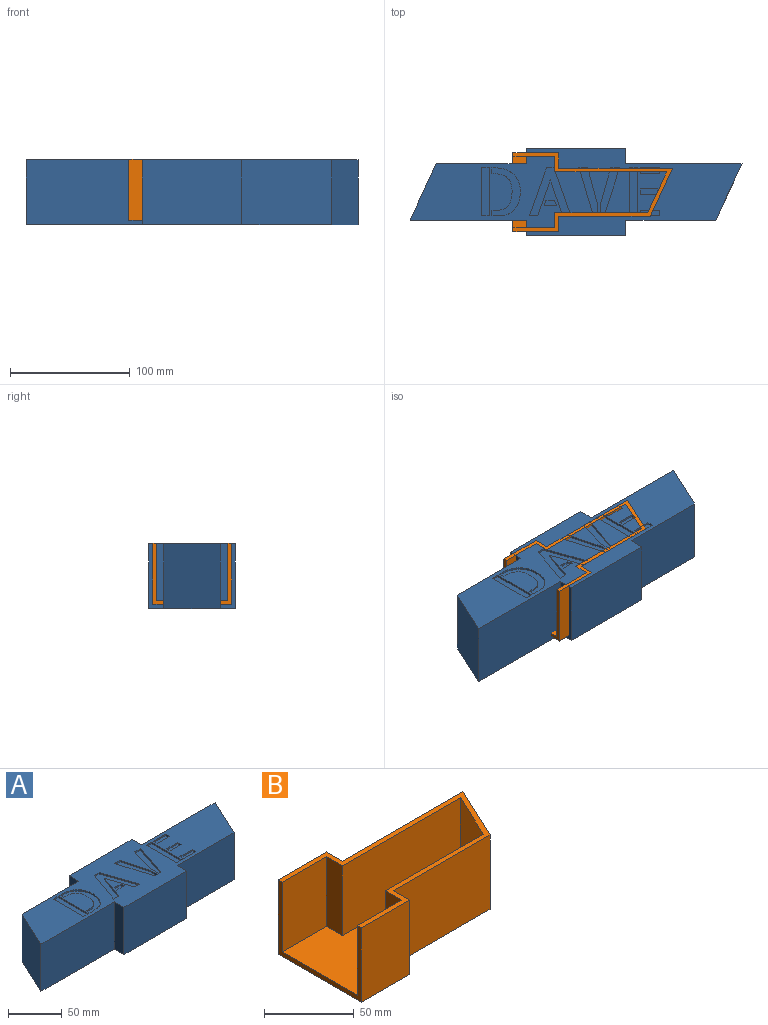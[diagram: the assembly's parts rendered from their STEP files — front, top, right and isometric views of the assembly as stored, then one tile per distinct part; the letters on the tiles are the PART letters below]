
ASSEMBLY  parts=2 mates=1
PART A: 100 faces, bbox 276.7x72.4x54 mm
  f0: plane 276.71x72.36mm, normal (0,0,1), area 11913.1mm2, adj f2,f3,f4,f5,f6,f7,f8,f9
  f1: plane 276.71x72.36mm, normal (0,0,-1), area 2063.9mm2, adj f2,f3,f4,f5,f6,f7,f8,f9
  f2: plane 83.06x53.98mm, normal (0,1,0), area 4483.1mm2, adj f0,f1,f3,f13
  f3: plane 53.98x12.7mm, normal (-1,0,0), area 685.5mm2, adj f0,f1,f2,f4
  f4: plane 74.93x53.98mm, normal (0,1,0), area 4044.3mm2, adj f0,f1,f3,f5
  f5: plane 53.98x46.96mm, normal (-0.91,0.42,0), area 2796.8mm2, adj f0,f1,f4,f6
  f6: plane 96.83x53.98mm, normal (0,-1,0), area 5226.3mm2, adj f0,f1,f5,f7
  f7: plane 53.98x12.7mm, normal (-1,0,0), area 685.5mm2, adj f0,f1,f6,f8
  f8: plane 83.06x53.98mm, normal (0,-1,0), area 4483.1mm2, adj f0,f1,f7,f9
  f9: plane 53.98x12.7mm, normal (1,0,0), area 685.5mm2, adj f0,f1,f8,f10
  f10: plane 74.93x53.98mm, normal (0,-1,0), area 4044.3mm2, adj f0,f1,f9,f11
  f11: plane 53.98x46.96mm, normal (0.91,-0.42,0), area 2796.8mm2, adj f0,f1,f10,f12
  f12: plane 96.83x53.98mm, normal (0,1,0), area 5226.3mm2, adj f0,f1,f11,f13
  f13: plane 53.98x12.7mm, normal (1,0,0), area 685.5mm2, adj f0,f1,f2,f12
  f14: plane 76.71x50.8mm, normal (0,-1,0), area 3896.8mm2, adj f1,f15,f25,f26
  f15: plane 50.8x12.7mm, normal (1,0,0), area 645.2mm2, adj f1,f14,f16,f26
  f16: plane 76.08x50.8mm, normal (0,-1,0), area 3865mm2, adj f1,f15,f17,f26
  f17: plane 50.8x40.61mm, normal (0.91,-0.42,0), area 2276.3mm2, adj f1,f16,f18,f26
  f18: plane 95.02x50.8mm, normal (0,1,0), area 4827mm2, adj f1,f17,f19,f26
  f19: plane 50.8x12.7mm, normal (1,0,0), area 645.2mm2, adj f1,f18,f20,f26
  f20: plane 76.71x50.8mm, normal (0,1,0), area 3896.8mm2, adj f1,f19,f21,f26
  f21: plane 50.8x12.7mm, normal (-1,0,0), area 645.2mm2, adj f1,f20,f22,f26
  f22: plane 76.08x50.8mm, normal (0,1,0), area 3865mm2, adj f1,f21,f23,f26
  f23: plane 50.8x40.61mm, normal (-0.91,0.42,0), area 2276.3mm2, adj f1,f22,f24,f26
  f24: plane 95.02x50.8mm, normal (0,-1,0), area 4827mm2, adj f1,f23,f25,f26
  f25: plane 50.8x12.7mm, normal (-1,0,0), area 645.2mm2, adj f1,f14,f24,f26
  f26: plane 266.75x66.01mm, normal (0,0,-1), area 12012.3mm2, adj f14,f15,f16,f17,f18,f19,f20,f21
  f27: plane 7.44x1.59mm, normal (0,-1,0), area 11.8mm2, adj f0,f28,f31,f32
  f28: plane 40.27x12.44mm, normal (0.96,0.3,0), area 66.9mm2, adj f0,f27,f29,f32
  f29: plane 3.43x1.59mm, normal (0,1,0), area 5.4mm2, adj f0,f28,f30,f32
  f30: plane 8.86x1.59mm, normal (-1,0,0), area 14.1mm2, adj f0,f29,f31,f32
  f31: plane 31.41x8.43mm, normal (-0.97,-0.26,0), area 51.6mm2, adj f0,f27,f30,f32
  f32: plane 40.27x15.87mm, normal (0,0,1), area 256.2mm2, adj f27,f28,f29,f30,f31
  f33: plane 4.41x1.59mm, normal (-0.94,-0.34,0), area 7.4mm2, adj f0,f34,f36,f37
  f34: plane 7.29x1.59mm, normal (0,-1,0), area 11.6mm2, adj f0,f33,f35,f37
  f35: plane 4.41x1.59mm, normal (0.95,-0.33,0), area 7.4mm2, adj f0,f34,f36,f37
  f36: plane 10.38x1.59mm, normal (0,1,0), area 16.5mm2, adj f0,f33,f35,f37
  f37: plane 10.38x4.41mm, normal (0,0,1), area 38.9mm2, adj f33,f34,f35,f36
  f38: plane 6.74x1.59mm, normal (0,1,0), area 10.7mm2, adj f0,f39,f44,f45
  f39: plane 40x13.91mm, normal (-0.94,-0.33,0), area 67.2mm2, adj f0,f38,f40,f45
  f40: plane 6.47x1.59mm, normal (0,-1,0), area 10.3mm2, adj f0,f39,f41,f45
  f41: plane 40x14.02mm, normal (0.94,-0.33,0), area 67.3mm2, adj f0,f40,f42,f45
  f42: plane 6.79x1.59mm, normal (0,1,0), area 10.8mm2, adj f0,f41,f43,f45
  f43: plane 30x10.49mm, normal (-0.94,0.33,0), area 50.5mm2, adj f0,f42,f44,f45
  f44: plane 30x10.38mm, normal (0.95,0.33,0), area 50.4mm2, adj f0,f38,f43,f45
  f45: plane 40x34.4mm, normal (0,0,1), area 504.3mm2, adj f38,f39,f40,f41,f42,f43,f44
  f46: extruded ~8.88x1.6mm, area 14.4mm2, adj f0,f47,f67,f68
  f47: plane 3.32x1.59mm, normal (0,-1,0), area 5.3mm2, adj f0,f46,f48,f68
  f48: plane 4.94x1.59mm, normal (1,0,0), area 7.8mm2, adj f0,f47,f49,f68
  f49: plane 1.59x1.58mm, normal (0,1,0), area 2.5mm2, adj f0,f48,f50,f68
  f50: extruded ~7.6x1.59mm, area 12.3mm2, adj f0,f49,f51,f68
  f51: extruded ~4.65x3.21mm, area 9mm2, adj f0,f50,f52,f68
  f52: extruded ~4.43x2.31mm, area 8mm2, adj f0,f51,f53,f68
  f53: extruded ~4.95x1.59mm, area 7.9mm2, adj f0,f52,f54,f68
  f54: extruded ~12.28x2.93mm, area 20.3mm2, adj f0,f53,f55,f68
  f55: extruded ~9.56x4.24mm, area 17.3mm2, adj f0,f54,f56,f68
  f56: plane 4.24x1.59mm, normal (0,-1,0), area 6.7mm2, adj f0,f55,f57,f68
  f57: plane 4.78x1.59mm, normal (1,0,0), area 7.6mm2, adj f0,f56,f58,f68
  f58: plane 6.42x1.59mm, normal (0,1,0), area 10.2mm2, adj f0,f57,f59,f68
  f59: extruded ~2.33x1.59mm, area 3.7mm2, adj f0,f58,f60,f68
  f60: extruded ~3.48x1.59mm, area 5.7mm2, adj f0,f59,f61,f68
  f61: extruded ~3.94x2.04mm, area 7.1mm2, adj f0,f60,f62,f68
  f62: extruded ~3.72x3.67mm, area 8.3mm2, adj f0,f61,f63,f68
  f63: extruded ~5.87x2.69mm, area 10.3mm2, adj f0,f62,f64,f68
  f64: extruded ~8.45x1.59mm, area 13.6mm2, adj f0,f63,f65,f68
  f65: extruded ~6.99x1.59mm, area 11.3mm2, adj f0,f64,f66,f68
  f66: extruded ~6.06x3.78mm, area 11.4mm2, adj f0,f65,f67,f68
  f67: extruded ~6.36x4.27mm, area 12.2mm2, adj f0,f46,f66,f68
  f68: plane 40.05x23.59mm, normal (0,0,1), area 361.5mm2, adj f46,f47,f48,f49,f50,f51,f52,f53
  f69: plane 7.39x1.59mm, normal (0,-1,0), area 11.7mm2, adj f0,f70,f73,f74
  f70: plane 29.67x8.48mm, normal (0.96,-0.27,0), area 49mm2, adj f0,f69,f71,f74
  f71: plane 10.6x1.59mm, normal (1,0,0), area 16.8mm2, adj f0,f70,f72,f74
  f72: plane 2.83x1.59mm, normal (0,1,0), area 4.5mm2, adj f0,f71,f73,f74
  f73: plane 40.27x13.04mm, normal (-0.95,0.31,0), area 67.2mm2, adj f0,f69,f72,f74
  f74: plane 40.27x15.87mm, normal (0,0,1), area 250.7mm2, adj f69,f70,f71,f72,f73
  f75: plane 6.63x1.59mm, normal (0,-1,0), area 10.5mm2, adj f0,f76,f78,f79
  f76: plane 40.05x1.59mm, normal (1,0,0), area 63.6mm2, adj f0,f75,f77,f79
  f77: plane 6.63x1.59mm, normal (0,1,0), area 10.5mm2, adj f0,f76,f78,f79
  f78: plane 40.05x1.59mm, normal (-1,0,0), area 63.6mm2, adj f0,f75,f77,f79
  f79: plane 40.05x6.63mm, normal (0,0,1), area 265.4mm2, adj f75,f76,f77,f78
  f80: plane 14.5x1.59mm, normal (0,1,0), area 23mm2, adj f0,f81,f83,f84
  f81: plane 4.46x1.59mm, normal (-1,0,0), area 7.1mm2, adj f0,f80,f82,f84
  f82: plane 14.5x1.59mm, normal (0,-1,0), area 23mm2, adj f0,f81,f83,f84
  f83: plane 4.46x1.59mm, normal (1,0,0), area 7.1mm2, adj f0,f80,f82,f84
  f84: plane 14.5x4.46mm, normal (0,0,1), area 64.7mm2, adj f80,f81,f82,f83
  f85: plane 16.19x1.59mm, normal (0,-1,0), area 25.7mm2, adj f0,f86,f88,f89
  f86: plane 4.95x1.59mm, normal (1,0,0), area 7.9mm2, adj f0,f85,f87,f89
  f87: plane 16.19x1.59mm, normal (0,1,0), area 25.7mm2, adj f0,f86,f88,f89
  f88: plane 4.95x1.59mm, normal (-1,0,0), area 7.9mm2, adj f0,f85,f87,f89
  f89: plane 16.19x4.95mm, normal (0,0,1), area 80.1mm2, adj f85,f86,f87,f88
  f90: plane 4.94x1.59mm, normal (-1,0,0), area 7.8mm2, adj f0,f91,f93,f94
  f91: plane 16.19x1.59mm, normal (0,-1,0), area 25.7mm2, adj f0,f90,f92,f94
  f92: plane 4.94x1.59mm, normal (1,0,0), area 7.8mm2, adj f0,f91,f93,f94
  f93: plane 16.19x1.59mm, normal (0,1,0), area 25.7mm2, adj f0,f90,f92,f94
  f94: plane 16.19x4.94mm, normal (0,0,1), area 80mm2, adj f90,f91,f92,f93
  f95: plane 6.52x1.59mm, normal (0,-1,0), area 10.4mm2, adj f0,f96,f98,f99
  f96: plane 40.05x1.59mm, normal (1,0,0), area 63.6mm2, adj f0,f95,f97,f99
  f97: plane 6.52x1.59mm, normal (0,1,0), area 10.4mm2, adj f0,f96,f98,f99
  f98: plane 40.05x1.59mm, normal (-1,0,0), area 63.6mm2, adj f0,f95,f97,f99
  f99: plane 40.05x6.52mm, normal (0,0,1), area 261.2mm2, adj f95,f96,f97,f98
PART B: 18 faces, bbox 133.1x65.7x50.8 mm
  f0: plane 50.8x12.7mm, normal (1,0,0), area 645.2mm2, adj f1,f13,f15,f16
  f1: plane 76.2x50.8mm, normal (0,-1,0), area 3871mm2, adj f0,f2,f13,f16
  f2: plane 50.8x40.29mm, normal (0.91,-0.42,0), area 2258.1mm2, adj f1,f3,f13,f16
  f3: plane 94.99x50.8mm, normal (0,1,0), area 4825.3mm2, adj f2,f4,f13,f16
  f4: plane 50.8x12.7mm, normal (1,0,0), area 645.2mm2, adj f3,f13,f14,f16
  f5: plane 47.63x12.7mm, normal (-1,0,0), area 604.8mm2, adj f6,f10,f11,f16
  f6: plane 93.18x47.63mm, normal (0,-1,0), area 4437.5mm2, adj f5,f7,f10,f16
  f7: plane 47.63x33.94mm, normal (-0.91,0.42,0), area 1783.2mm2, adj f6,f8,f10,f16
  f8: plane 77.35x47.63mm, normal (0,1,0), area 3683.9mm2, adj f7,f9,f10,f16
  f9: plane 47.63x12.7mm, normal (-1,0,0), area 604.8mm2, adj f8,f10,f12,f16
  f10: plane 128.1x59.34mm, normal (0,0,1), area 4965.8mm2, adj f5,f6,f7,f8,f9,f11,f12,f17
  f11: plane 47.63x34.93mm, normal (0,-1,0), area 1663.3mm2, adj f5,f10,f16,f17
  f12: plane 47.63x34.93mm, normal (0,1,0), area 1663.3mm2, adj f9,f10,f16,f17
  f13: plane 133.09x65.69mm, normal (0,0,-1), area 5950.7mm2, adj f0,f1,f2,f3,f4,f14,f15,f17
  f14: plane 50.8x38.1mm, normal (0,1,0), area 1935.5mm2, adj f4,f13,f16,f17
  f15: plane 50.8x38.1mm, normal (0,-1,0), area 1935.5mm2, adj f0,f13,f16,f17
  f16: plane 133.09x65.69mm, normal (0,0,1), area 985mm2, adj f0,f1,f2,f3,f4,f5,f6,f7
  f17: plane 65.69x50.8mm, normal (-1,0,0), area 511mm2, adj f10,f11,f12,f13,f14,f15,f16
PLACE A t=(-60.72,-150.86,-57.78)mm
PLACE B t=(-108,-147.83,-54.31)mm fixed
MATE slider A.f26 <-> B.f10  axis (0,0,-1) through (-55.45,-147.52,-6.98)mm
